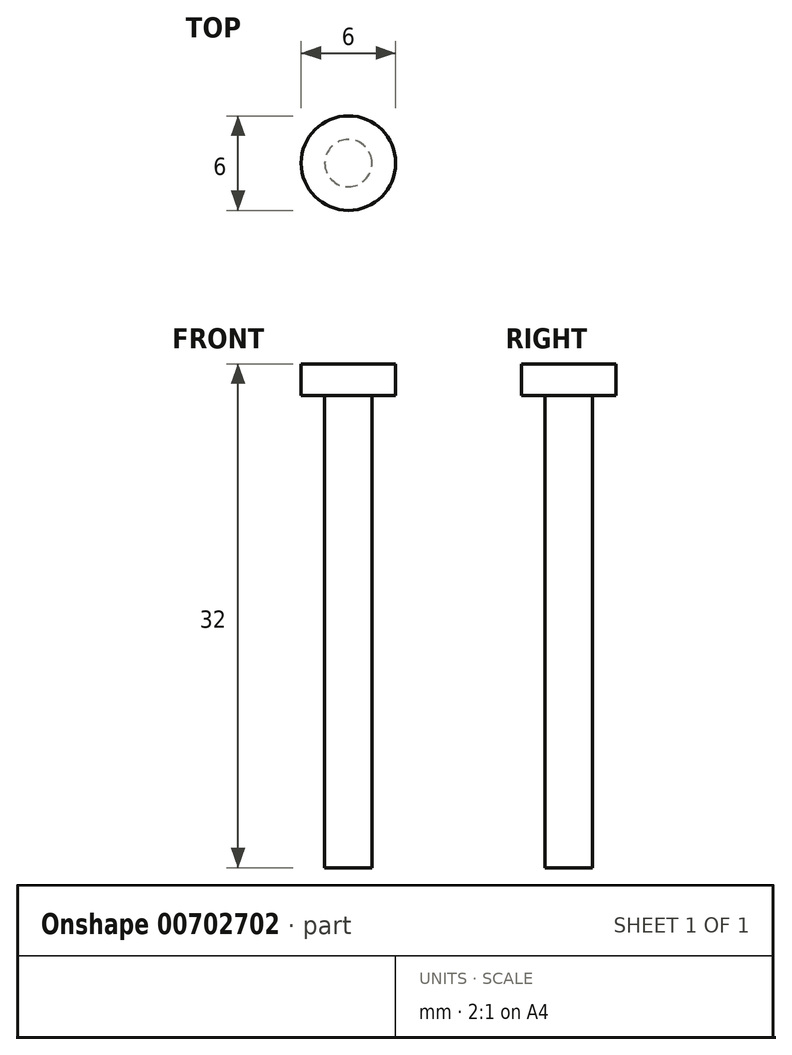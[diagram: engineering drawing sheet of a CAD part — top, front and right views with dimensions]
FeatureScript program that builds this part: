
annotation { "Feature Type Name" : "Feature", "Feature Type Description" : "" }
export const myFeature = defineFeature(function(context is Context, id is Id, definition is map)
    precondition{}
    {
        {
            var Q0;
            Q0=qCreatedBy(makeId("Front.planeOp"),FACE);
            var sketch = newSketch(context, id + "F0", { "sketchPlane" : qUnion([Q0])});
            skLineSegment(sketch, "E0", {"start": v(-1.5, 24.67) * mm, "end": v(1.5, 24.67) * mm});
            skLineSegment(sketch, "E1", {"start": v(1.5, 24.67) * mm, "end": v(1.5, 22.67) * mm});
            skLineSegment(sketch, "E2", {"start": v(1.5, 22.67) * mm, "end": v(0, 22.67) * mm});
            skLineSegment(sketch, "E3", {"start": v(0, 22.67) * mm, "end": v(0, -7.33) * mm});
            skLineSegment(sketch, "E4", {"start": v(0, -7.33) * mm, "end": v(-1.5, -7.33) * mm});
            skLineSegment(sketch, "E5", {"start": v(-1.5, -7.33) * mm, "end": v(-1.5, 24.67) * mm});
            skSolve(sketch);
        }
        {
            var Q0;
            Q0=makeQuery(id+"F0.imprint","IMPRINT",FACE,{"disambiguationData":[TD([[makeQuery(id+"F0.imprint","IMPRINT",EDGE,{"derivedFrom":sQuery(id+"F0.wireOp",EDGE,"E0")}),-1.0]])]});
            var Q1;
            Q1=sQuery(id+"F0.wireOp",EDGE,"E5");
            revolve(context, id + "F1", {"surfaceOperationType" : NewSurfaceOperationType.NEW, "entities" : qUnion([Q0]), "axis" : qUnion([Q1]), "revolveType" : RevolveType.FULL});
        }
    });
